# Revit family: Plumbing_Joints_Aignep_Saddle-Clamp-Connector-90240
name_source: partatom
category: Pipe Fittings
revit_build: Autodesk Revit 2018 (Build: 20170223_1515(x64)
units: mm (PartAtom-declared; Revit-internal decimal feet)

## family parameters
Always vertical = Yes
Cut with Voids When Loaded = No
OmniClass Number = 23.27.43.00
Part Type = Tee
Round Connector Dimension = Use Diameter
Shared = No
Work Plane-Based = No

## types (1)
- 90240
    Assembly Code = D2040100
    BIMobject category = Joints
    Description = Saddle clamp connector
    Design country = Italy
    Edition number = 1
    IFC Classification = Pipe Fitting
    Keynote = 15410
    Lookup Table Name = Tee - 90240
    Manufacturer = Aignep Spa
    Manufacturer country = Italy
    Manufacturer name = Aignep Spa
    Material main = Brass
    Model = 90240
    OmniClass Code = 23-27 43 00
    OmniClass Description = Pipe Fittings
    Product Guid = 00a60b4e-ab84-47b8-8dff-073ddd7285eb
    Product Material = AIGNEP - Brass - Yellow
    Product SKU = Saddle-clamp-connector-90240
    Product certification = https://www.aignep.com
    Product data url = https://www.bimobject.com
    Product family = INFINITY
    Product group = Fittings
    Product name = Saddle clamp connector - 90240
    Product url = https://www.aignep.com
    QR code = https://www.bimobject.com
    URL = https://www.aignep.com

## geometry (parser evidence)
native form markers: Sweep x1
no freeform markers — native parametric forms only
